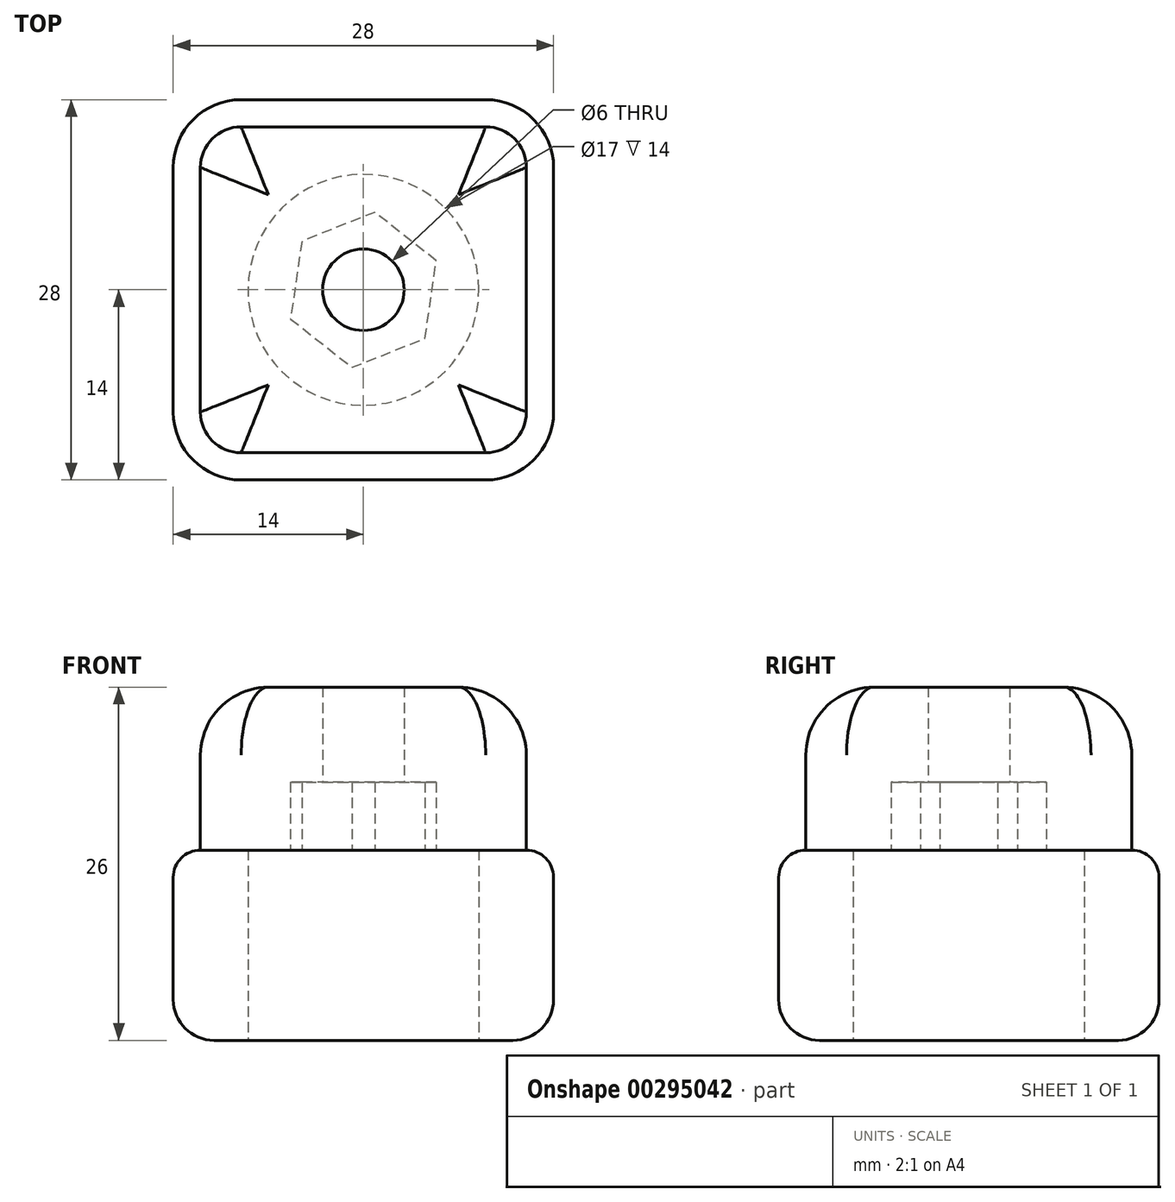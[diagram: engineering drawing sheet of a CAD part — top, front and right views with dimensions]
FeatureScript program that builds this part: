
annotation { "Feature Type Name" : "Feature", "Feature Type Description" : "" }
export const myFeature = defineFeature(function(context is Context, id is Id, definition is map)
    precondition{}
    {
        {
            var Q0;
            Q0=qCreatedBy(makeId("Top.planeOp"),FACE);
            var sketch = newSketch(context, id + "F0", { "sketchPlane" : qUnion([Q0])});
            skLineSegment(sketch, "E0.bottom", {"start": v(14, 14) * mm, "end": v(-14, 14) * mm});
            skLineSegment(sketch, "E0.top", {"start": v(14, -14) * mm, "end": v(-14, -14) * mm});
            skLineSegment(sketch, "E0.left", {"start": v(14, 14) * mm, "end": v(14, -14) * mm});
            skLineSegment(sketch, "E0.right", {"start": v(-14, 14) * mm, "end": v(-14, -14) * mm});
            skPoint(sketch, "E0.middle", {"position": v(0, 0) * mm});
            skSolve(sketch);
        }
        {
            var Q0;
            Q0=qSketchRegion(id+"F0",true);
            extrude(context, id + "F1", {"entities" : qUnion([Q0]), "depth" : 14 * mm});
        }
        {
            var Q0;
            Q0=makeQuery(id+"F1.opExtrude","CAP_FACE",FACE,{"disambiguationData":[OSD([sQuery(id+"F0.wireOp",EDGE,"E0.bottom"),sQuery(id+"F0.wireOp",EDGE,"E0.top"),sQuery(id+"F0.wireOp",EDGE,"E0.left"),sQuery(id+"F0.wireOp",EDGE,"E0.right")])],"isStart":false});
            var sketch = newSketch(context, id + "F2", { "sketchPlane" : qUnion([Q0])});
            skLineSegment(sketch, "E1.bottom", {"start": v(12, 12) * mm, "end": v(-12, 12) * mm});
            skLineSegment(sketch, "E1.top", {"start": v(12, -12) * mm, "end": v(-12, -12) * mm});
            skLineSegment(sketch, "E1.left", {"start": v(12, 12) * mm, "end": v(12, -12) * mm});
            skLineSegment(sketch, "E1.right", {"start": v(-12, 12) * mm, "end": v(-12, -12) * mm});
            skSolve(sketch);
        }
        {
            var Q0;
            Q0=makeQuery(id+"F2.imprint","IMPRINT",FACE,{"disambiguationData":[TD([[makeQuery(id+"F2.imprint","IMPRINT",EDGE,{"derivedFrom":sQuery(id+"F2.wireOp",EDGE,"E1.bottom")}),1.0]])]});
            extrude(context, id + "F3", {"entities" : qUnion([Q0]), "operationType" : NewBodyOperationType.ADD, "depth" : 12 * mm});
        }
        {
            var Q0;
            Q0=makeQuery(id+"F1.opExtrude","CAP_FACE",FACE,{"disambiguationData":[OSD([sQuery(id+"F0.wireOp",EDGE,"E0.bottom"),sQuery(id+"F0.wireOp",EDGE,"E0.top"),sQuery(id+"F0.wireOp",EDGE,"E0.left"),sQuery(id+"F0.wireOp",EDGE,"E0.right")])],"isStart":true});
            var sketch = newSketch(context, id + "F4", { "sketchPlane" : qUnion([Q0])});
            skCircle(sketch, "E2", {"center": v(0, 0) * mm, "radius": 8.5 * mm});
            skSolve(sketch);
        }
        {
            var Q0;
            Q0=makeQuery(id+"F4.imprint","IMPRINT",FACE,{"disambiguationData":[TD([[makeQuery(id+"F4.imprint","IMPRINT",EDGE,{"derivedFrom":sQuery(id+"F4.wireOp",EDGE,"E2")}),1.0]])]});
            extrude(context, id + "F5", {"entities" : qUnion([Q0]), "operationType" : NewBodyOperationType.REMOVE, "oppositeDirection" : true, "depth" : 14 * mm});
        }
        {
            var Q0;
            Q0=makeQuery(id+"F1.opExtrude","CAP_FACE",FACE,{"disambiguationData":[OSD([sQuery(id+"F0.wireOp",EDGE,"E0.bottom"),sQuery(id+"F0.wireOp",EDGE,"E0.top"),sQuery(id+"F0.wireOp",EDGE,"E0.left"),sQuery(id+"F0.wireOp",EDGE,"E0.right")])],"isStart":true});
            var sketch = newSketch(context, id + "F6", { "sketchPlane" : qUnion([Q0])});
            skCircle(sketch, "E3", {"center": v(0, 0) * mm, "radius": 3 * mm});
            skSolve(sketch);
        }
        {
            var Q0;
            Q0=qSketchRegion(id+"F6",true);
            extrude(context, id + "F7", {"entities" : qUnion([Q0]), "operationType" : NewBodyOperationType.REMOVE, "endBound" : BoundingType.THROUGH_ALL, "oppositeDirection" : true, "depth" : 25 * mm});
        }
        {
            var Q0;
            Q0=makeQuery(id+"F1.opExtrude","SWEPT_EDGE",EDGE,{"disambiguationData":[OSD([sQuery(id+"F0.wireOp",EDGE,"E0.bottom"),sQuery(id+"F0.wireOp",EDGE,"E0.left")])]});
            var Q1;
            Q1=makeQuery(id+"F1.opExtrude","SWEPT_EDGE",EDGE,{"disambiguationData":[OSD([sQuery(id+"F0.wireOp",EDGE,"E0.bottom"),sQuery(id+"F0.wireOp",EDGE,"E0.right")])]});
            var Q2;
            Q2=makeQuery(id+"F1.opExtrude","SWEPT_EDGE",EDGE,{"disambiguationData":[OSD([sQuery(id+"F0.wireOp",EDGE,"E0.top"),sQuery(id+"F0.wireOp",EDGE,"E0.left")])]});
            var Q3;
            Q3=makeQuery(id+"F1.opExtrude","SWEPT_EDGE",EDGE,{"disambiguationData":[OSD([sQuery(id+"F0.wireOp",EDGE,"E0.top"),sQuery(id+"F0.wireOp",EDGE,"E0.right")])]});
            fillet(context, id + "F8", {"entities" : qUnion([Q0, Q1, Q2, Q3]), "radius" : 5 * mm, "tangentPropagation" : true, "allowEdgeOverflow" : false});
        }
        {
            var Q0;
            Q0=makeQuery(id+"F3.opExtrude","SWEPT_EDGE",EDGE,{"disambiguationData":[OSD([sQuery(id+"F2.wireOp",EDGE,"E1.bottom"),sQuery(id+"F2.wireOp",EDGE,"E1.right")])]});
            var Q1;
            Q1=makeQuery(id+"F3.opExtrude","SWEPT_EDGE",EDGE,{"disambiguationData":[OSD([sQuery(id+"F2.wireOp",EDGE,"E1.top"),sQuery(id+"F2.wireOp",EDGE,"E1.right")])]});
            var Q2;
            Q2=makeQuery(id+"F3.opExtrude","SWEPT_EDGE",EDGE,{"disambiguationData":[OSD([sQuery(id+"F2.wireOp",EDGE,"E1.top"),sQuery(id+"F2.wireOp",EDGE,"E1.left")])]});
            var Q3;
            Q3=makeQuery(id+"F3.opExtrude","SWEPT_EDGE",EDGE,{"disambiguationData":[OSD([sQuery(id+"F2.wireOp",EDGE,"E1.bottom"),sQuery(id+"F2.wireOp",EDGE,"E1.left")])]});
            fillet(context, id + "F9", {"entities" : qUnion([Q0, Q1, Q2, Q3]), "radius" : 3 * mm, "tangentPropagation" : true, "allowEdgeOverflow" : false});
        }
        {
            var Q0;
            Q0=makeQuery(id+"F1.opExtrude","SWEPT_FACE",FACE,{"disambiguationData":[OSD([sQuery(id+"F0.wireOp",EDGE,"E0.left")])]});
            var sketch = newSketch(context, id + "F10", { "sketchPlane" : qUnion([Q0])});
            skLineSegment(sketch, "E4", {"start": v(9, 0) * mm, "end": v(-9, 14) * mm, "construction": true});
            skCircle(sketch, "E5.cCircle", {"center": v(0, 7) * mm, "radius": 3.5 * mm, "construction": true});
            skLineSegment(sketch, "E5.0", {"start": v(-1.59, 3.28) * mm, "end": v(-4.01, 6.52) * mm});
            skLineSegment(sketch, "E5.1", {"start": v(-4.01, 6.52) * mm, "end": v(-2.42, 10.23) * mm});
            skLineSegment(sketch, "E5.2", {"start": v(-2.42, 10.23) * mm, "end": v(1.59, 10.72) * mm});
            skLineSegment(sketch, "E5.3", {"start": v(1.59, 10.72) * mm, "end": v(4.01, 7.48) * mm});
            skLineSegment(sketch, "E5.4", {"start": v(4.01, 7.48) * mm, "end": v(2.42, 3.77) * mm});
            skLineSegment(sketch, "E5.5", {"start": v(2.42, 3.77) * mm, "end": v(-1.59, 3.28) * mm});
            skPoint(sketch, "E5.0.midPoint", {"position": v(-2.8, 4.9) * mm});
            skSolve(sketch);
        }
        {
            var Q0;
            Q0=makeQuery(id+"F1.opExtrude","SWEPT_FACE",FACE,{"disambiguationData":[OSD([sQuery(id+"F0.wireOp",EDGE,"E0.top")])]});
            var sketch = newSketch(context, id + "F11", { "sketchPlane" : qUnion([Q0])});
            skLineSegment(sketch, "E6", {"start": v(9, 0) * mm, "end": v(-9, 14) * mm, "construction": true});
            skCircle(sketch, "E7.cCircle", {"center": v(0, 7) * mm, "radius": 3.5 * mm, "construction": true});
            skLineSegment(sketch, "E7.0", {"start": v(-1.59, 3.28) * mm, "end": v(-4.01, 6.52) * mm});
            skLineSegment(sketch, "E7.1", {"start": v(-4.01, 6.52) * mm, "end": v(-2.42, 10.23) * mm});
            skLineSegment(sketch, "E7.2", {"start": v(-2.42, 10.23) * mm, "end": v(1.59, 10.72) * mm});
            skLineSegment(sketch, "E7.3", {"start": v(1.59, 10.72) * mm, "end": v(4.01, 7.48) * mm});
            skLineSegment(sketch, "E7.4", {"start": v(4.01, 7.48) * mm, "end": v(2.42, 3.77) * mm});
            skLineSegment(sketch, "E7.5", {"start": v(2.42, 3.77) * mm, "end": v(-1.59, 3.28) * mm});
            skPoint(sketch, "E7.0.midPoint", {"position": v(-2.8, 4.9) * mm});
            skSolve(sketch);
        }
        {
            var Q0;
            {var subQ0=sQuery(id+"F0.wireOp",EDGE,"E0.right");var subQ1=sQuery(id+"F0.wireOp",EDGE,"E0.bottom");Q0=makeQuery(id+"F8.opFillet","BLEND_EDGE",EDGE,{"blendedFrom":[makeQuery(id+"F1.opExtrude","SWEPT_EDGE",EDGE,{"disambiguationData":[OSD([subQ1,subQ0])]}),makeQuery(id+"F1.opExtrude","CAP_FACE",FACE,{"disambiguationData":[OSD([subQ1,sQuery(id+"F0.wireOp",EDGE,"E0.top"),sQuery(id+"F0.wireOp",EDGE,"E0.left"),subQ0])],"isStart":true})],"blendedInto":[makeQuery(id+"F1.opExtrude","CAP_FACE",FACE,{"disambiguationData":[OSD([subQ1,sQuery(id+"F0.wireOp",EDGE,"E0.top"),sQuery(id+"F0.wireOp",EDGE,"E0.left"),subQ0])],"isStart":true})]});}
            fillet(context, id + "F12", {"entities" : qUnion([Q0]), "radius" : 3 * mm, "tangentPropagation" : true, "allowEdgeOverflow" : false});
        }
        {
            var Q0;
            {var subQ0=sQuery(id+"F0.wireOp",EDGE,"E0.right");var subQ1=sQuery(id+"F0.wireOp",EDGE,"E0.top");Q0=makeQuery(id+"F8.opFillet","BLEND_EDGE",EDGE,{"blendedFrom":[makeQuery(id+"F1.opExtrude","SWEPT_EDGE",EDGE,{"disambiguationData":[OSD([subQ1,subQ0])]}),makeQuery(id+"F1.opExtrude","CAP_FACE",FACE,{"disambiguationData":[OSD([sQuery(id+"F0.wireOp",EDGE,"E0.bottom"),subQ1,sQuery(id+"F0.wireOp",EDGE,"E0.left"),subQ0])],"isStart":false})],"blendedInto":[makeQuery(id+"F1.opExtrude","CAP_FACE",FACE,{"disambiguationData":[OSD([sQuery(id+"F0.wireOp",EDGE,"E0.bottom"),subQ1,sQuery(id+"F0.wireOp",EDGE,"E0.left"),subQ0])],"isStart":false})]});}
            fillet(context, id + "F13", {"entities" : qUnion([Q0]), "radius" : 2 * mm, "tangentPropagation" : true, "allowEdgeOverflow" : false});
        }
        {
            var Q0;
            {var subQ0=sQuery(id+"F2.wireOp",EDGE,"E1.right");var subQ1=sQuery(id+"F2.wireOp",EDGE,"E1.top");Q0=makeQuery(id+"F9.opFillet","BLEND_EDGE",EDGE,{"blendedFrom":[makeQuery(id+"F3.opExtrude","SWEPT_EDGE",EDGE,{"disambiguationData":[OSD([subQ1,subQ0])]}),makeQuery(id+"F3.opExtrude","CAP_FACE",FACE,{"disambiguationData":[OSD([sQuery(id+"F2.wireOp",EDGE,"E1.bottom"),subQ1,sQuery(id+"F2.wireOp",EDGE,"E1.left"),subQ0])],"isStart":false})],"blendedInto":[makeQuery(id+"F3.opExtrude","CAP_FACE",FACE,{"disambiguationData":[OSD([sQuery(id+"F2.wireOp",EDGE,"E1.bottom"),subQ1,sQuery(id+"F2.wireOp",EDGE,"E1.left"),subQ0])],"isStart":false})]});}
            fillet(context, id + "F14", {"entities" : qUnion([Q0]), "radius" : 5 * mm, "tangentPropagation" : true, "allowEdgeOverflow" : false});
        }
        {
            var Q0;
            Q0=makeQuery(id+"F5.boolean.opBoolean","COPY",FACE,{"derivedFrom":makeQuery(id+"F5.opExtrude","CAP_FACE",FACE,{"disambiguationData":[OSD([sQuery(id+"F4.wireOp",EDGE,"E2")])],"isStart":false})});
            var sketch = newSketch(context, id + "F15", { "sketchPlane" : qUnion([Q0])});
            skCircle(sketch, "E8", {"center": v(0, 0) * mm, "radius": 4.03 * mm, "construction": true});
            skCircle(sketch, "E9.cCircle", {"center": v(0, 0) * mm, "radius": 5 * mm, "construction": true});
            skLineSegment(sketch, "E9.0", {"start": v(-4.53, -3.58) * mm, "end": v(-5.36, 2.14) * mm});
            skLineSegment(sketch, "E9.1", {"start": v(-5.36, 2.14) * mm, "end": v(-0.83, 5.71) * mm});
            skLineSegment(sketch, "E9.2", {"start": v(-0.83, 5.71) * mm, "end": v(4.53, 3.58) * mm});
            skLineSegment(sketch, "E9.3", {"start": v(4.53, 3.58) * mm, "end": v(5.36, -2.14) * mm});
            skLineSegment(sketch, "E9.4", {"start": v(5.36, -2.14) * mm, "end": v(0.83, -5.71) * mm});
            skLineSegment(sketch, "E9.5", {"start": v(0.83, -5.71) * mm, "end": v(-4.53, -3.58) * mm});
            skPoint(sketch, "E9.0.midPoint", {"position": v(-4.95, -0.72) * mm});
            skSolve(sketch);
        }
        {
            var Q0;
            Q0 = qSketchRegion(id + "F15", true);
            extrude(context, id + "F16", {"entities" : qUnion([Q0]), "operationType" : NewBodyOperationType.REMOVE, "oppositeDirection" : true, "depth" : 5 * mm});
        }
    });
